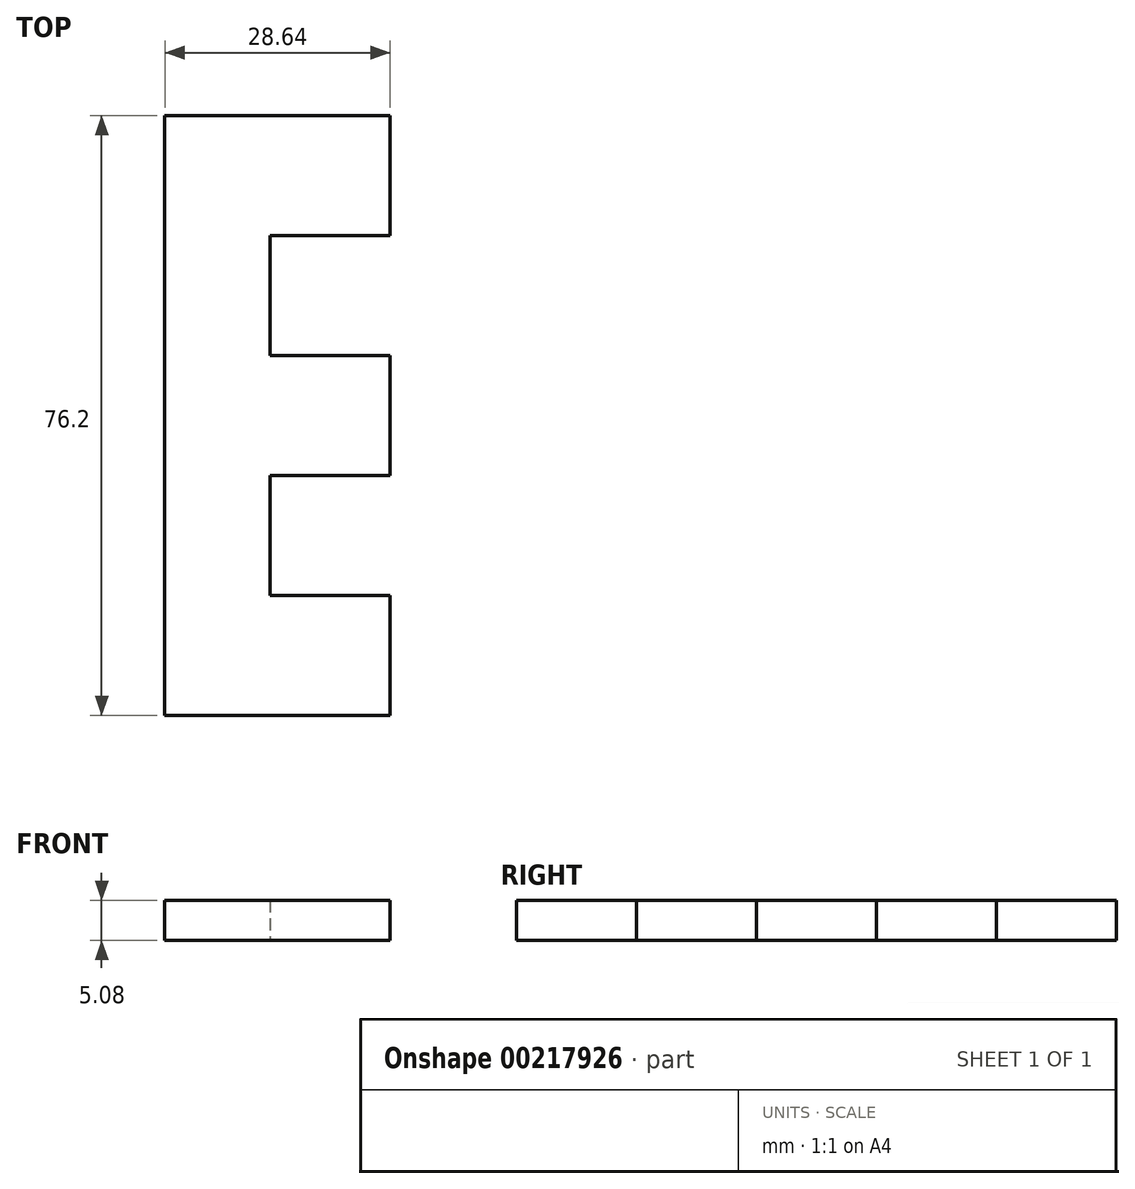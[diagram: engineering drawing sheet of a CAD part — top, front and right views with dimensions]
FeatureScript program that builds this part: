
annotation { "Feature Type Name" : "Feature", "Feature Type Description" : "" }
export const myFeature = defineFeature(function(context is Context, id is Id, definition is map)
    precondition{}
    {
        {
            var Q0;
            Q0=qCreatedBy(makeId("Top.planeOp"),FACE);
            var sketch = newSketch(context, id + "F0", { "sketchPlane" : qUnion([Q0])});
            skLineSegment(sketch, "E0", {"start": v(-28.64, 45.81) * mm, "end": v(0, 45.81) * mm});
            skLineSegment(sketch, "E1", {"start": v(0, 45.81) * mm, "end": v(0, 30.57) * mm});
            skLineSegment(sketch, "E2", {"start": v(0, 30.57) * mm, "end": v(-15.24, 30.57) * mm});
            skLineSegment(sketch, "E3", {"start": v(-15.24, 30.57) * mm, "end": v(-15.24, 15.33) * mm});
            skLineSegment(sketch, "E4", {"start": v(-15.24, 15.33) * mm, "end": v(0, 15.33) * mm});
            skLineSegment(sketch, "E5", {"start": v(0, 15.33) * mm, "end": v(0, 0.1) * mm});
            skLineSegment(sketch, "E6", {"start": v(0, 0.1) * mm, "end": v(-15.24, 0.1) * mm});
            skLineSegment(sketch, "E7", {"start": v(-15.24, 0.1) * mm, "end": v(-15.24, -15.15) * mm});
            skLineSegment(sketch, "E8", {"start": v(-15.24, -15.15) * mm, "end": v(0, -15.15) * mm});
            skLineSegment(sketch, "E9", {"start": v(0, -15.15) * mm, "end": v(0, -30.39) * mm});
            skLineSegment(sketch, "E10", {"start": v(-28.64, 45.81) * mm, "end": v(-28.64, -30.39) * mm});
            skLineSegment(sketch, "E11", {"start": v(-28.64, -30.39) * mm, "end": v(0, -30.39) * mm});
            skSolve(sketch);
        }
        {
            var Q0;
            Q0 = qSketchRegion(id + "F0", true);
            extrude(context, id + "F1", {"entities" : qUnion([Q0]), "endBound" : BoundingType.SYMMETRIC, "depth" : 5.08 * mm});
        }
    });
